FCSTD DOCUMENT  (FreeCAD 0.16R5332 (Git))
Label: Intrinisics
License: All rights reserved
LicenseURL: http://en.wikipedia.org/wiki/All_rights_reserved
objects: Part::Part2DObjectPython×10
note: 10 computed .brp shape members not serialized (recipe doc carries the construction recipe); baked Part::Feature solids carry a one-line shape summary decoded from their .brp

FEATURE [Part::Part2DObjectPython] Rectangle  # Draft 2D object (typed FeaturePython)
  ChamferSize = 0
  FilletRadius = 0
  Height = 30
  Length = 30
  MakeFace = false
  Placement = pos=(-10,-10,20) rot=(0,0,1;0rad)
FEATURE [Part::Part2DObjectPython] Line  # Draft 2D object (typed FeaturePython)
  ChamferSize = 0
  Closed = false
  End = (20,0,20)
  FilletRadius = 0
  Length = 20
  MakeFace = false
  Points = (2) [(0,0,20),(20,0,20)]
  Start = (0,0,20)
FEATURE [Part::Part2DObjectPython] Line001  # Draft 2D object (typed FeaturePython)
  ChamferSize = 0
  Closed = true
  End = (0,-10,20)
  FilletRadius = 0
  Length = 10
  MakeFace = false
  Points = (2) [(0,0,20),(0,-10,20)]
  Start = (0,0,20)
FEATURE [Part::Part2DObjectPython] Line002  label="ZAxis"  # Draft 2D object (typed FeaturePython)
  ChamferSize = 0
  Closed = false
  End = (0,0,50)
  FilletRadius = 0
  Length = 50
  MakeFace = false
  Points = (2) [(0,0,0),(0,0,50)]
  Start = (0,0,0)
FEATURE [Part::Part2DObjectPython] Line004  label="XAxis"  # Draft 2D object (typed FeaturePython)
  ChamferSize = 0
  Closed = false
  End = (50,0,0)
  FilletRadius = 0
  Length = 50
  MakeFace = false
  Points = (2) [(0,0,0),(50,0,0)]
  Start = (0,0,0)
FEATURE [Part::Part2DObjectPython] Line005  label="YAxis"  # Draft 2D object (typed FeaturePython)
  ChamferSize = 0
  Closed = false
  End = (0,50,0)
  FilletRadius = 0
  Length = 50
  MakeFace = false
  Points = (2) [(0,0,0),(0,50,0)]
  Start = (0,0,0)
FEATURE [Part::Part2DObjectPython] Line006  # Draft 2D object (typed FeaturePython)
  ChamferSize = 0
  Closed = false
  End = (20,7.5,20)
  FilletRadius = 0
  Length = 22.5
  MakeFace = false
  Points = (2) [(-2.5,7.5,20),(20,7.5,20)]
  Start = (-2.5,7.5,20)
FEATURE [Part::Part2DObjectPython] Line007  # Draft 2D object (typed FeaturePython)
  ChamferSize = 0
  Closed = false
  End = (-2.5,-10,20)
  FilletRadius = 0
  Length = 17.5
  MakeFace = false
  Points = (2) [(-2.5,7.5,20),(-2.5,-10,20)]
  Start = (-2.5,7.5,20)
FEATURE [Part::Part2DObjectPython] Line008  # Draft 2D object (typed FeaturePython)
  ChamferSize = 0
  Closed = false
  End = (-2.5,7.5,20)
  FilletRadius = 0
  Length = 21.5058
  MakeFace = false
  Points = (2) [(0,0,0),(-2.5,7.5,20)]
  Start = (0,0,0)
FEATURE [Part::Part2DObjectPython] Line009  # Draft 2D object (typed FeaturePython)
  ChamferSize = 0
  Closed = false
  End = (-5,15,40)
  FilletRadius = 0
  Length = 21.5058
  MakeFace = false
  Points = (2) [(-2.5,7.5,20),(-5,15,40)]
  Start = (-2.5,7.5,20)
